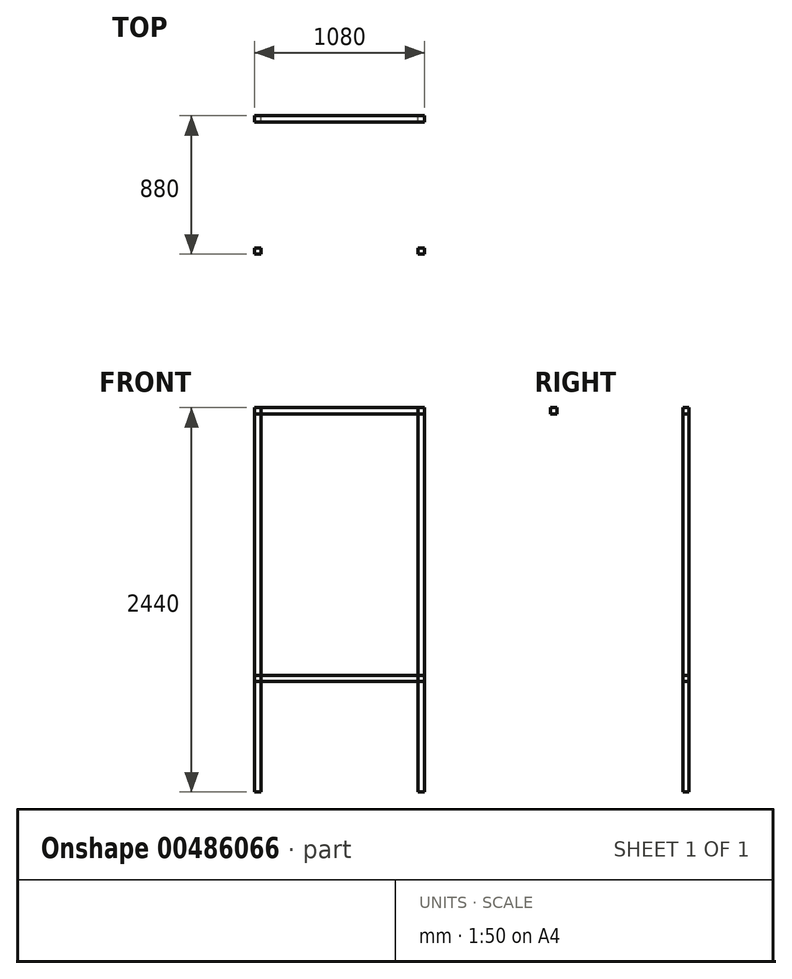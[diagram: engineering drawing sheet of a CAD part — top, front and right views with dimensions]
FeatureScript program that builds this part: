
annotation { "Feature Type Name" : "Feature", "Feature Type Description" : "" }
export const myFeature = defineFeature(function(context is Context, id is Id, definition is map)
    precondition{}
    {
        {
            var Q0;
            Q0=qCreatedBy(makeId("Top.planeOp"),FACE);
            var sketch = newSketch(context, id + "F0", { "sketchPlane" : qUnion([Q0])});
            skLineSegment(sketch, "E0.bottom", {"start": v(119.7, 99.7) * mm, "end": v(1119.7, 99.7) * mm});
            skLineSegment(sketch, "E0.left", {"start": v(119.7, 99.7) * mm, "end": v(119.7, 179.7) * mm});
            skLineSegment(sketch, "E0.right", {"start": v(1119.7, 99.7) * mm, "end": v(1119.7, 179.7) * mm});
            skLineSegment(sketch, "E1.bottom", {"start": v(1119.7, 99.7) * mm, "end": v(119.7, 99.7) * mm});
            skLineSegment(sketch, "E1.top", {"start": v(1119.7, 899.7) * mm, "end": v(119.7, 899.7) * mm});
            skLineSegment(sketch, "E1.left", {"start": v(1119.7, 99.7) * mm, "end": v(1119.7, 899.7) * mm});
            skLineSegment(sketch, "E1.right", {"start": v(119.7, 99.7) * mm, "end": v(119.7, 899.7) * mm});
            skLineSegment(sketch, "E2.0", {"start": v(1159.7, 939.7) * mm, "end": v(79.7, 939.7) * mm});
            skLineSegment(sketch, "E2.1", {"start": v(79.7, 59.7) * mm, "end": v(79.7, 939.7) * mm});
            skLineSegment(sketch, "E3.0", {"start": v(1159.7, 59.7) * mm, "end": v(79.7, 59.7) * mm});
            skLineSegment(sketch, "E4.0", {"start": v(1159.7, 59.7) * mm, "end": v(1159.7, 939.7) * mm});
            skLineSegment(sketch, "E5.bottom", {"start": v(79.7, 59.7) * mm, "end": v(119.7, 59.7) * mm});
            skLineSegment(sketch, "E5.top", {"start": v(79.7, 99.7) * mm, "end": v(119.7, 99.7) * mm});
            skLineSegment(sketch, "E5.left", {"start": v(79.7, 59.7) * mm, "end": v(79.7, 99.7) * mm});
            skLineSegment(sketch, "E5.right", {"start": v(119.7, 59.7) * mm, "end": v(119.7, 99.7) * mm});
            skLineSegment(sketch, "E6.bottom", {"start": v(1159.7, 59.7) * mm, "end": v(1119.7, 59.7) * mm});
            skLineSegment(sketch, "E6.top", {"start": v(1159.7, 99.7) * mm, "end": v(1119.7, 99.7) * mm});
            skLineSegment(sketch, "E6.left", {"start": v(1159.7, 59.7) * mm, "end": v(1159.7, 99.7) * mm});
            skLineSegment(sketch, "E6.right", {"start": v(1119.7, 59.7) * mm, "end": v(1119.7, 99.7) * mm});
            skLineSegment(sketch, "E7.bottom", {"start": v(1119.7, 899.7) * mm, "end": v(1159.7, 899.7) * mm});
            skLineSegment(sketch, "E7.top", {"start": v(1119.7, 939.7) * mm, "end": v(1159.7, 939.7) * mm});
            skLineSegment(sketch, "E7.left", {"start": v(1119.7, 899.7) * mm, "end": v(1119.7, 939.7) * mm});
            skLineSegment(sketch, "E7.right", {"start": v(1159.7, 899.7) * mm, "end": v(1159.7, 939.7) * mm});
            skLineSegment(sketch, "E8.bottom", {"start": v(119.7, 899.7) * mm, "end": v(79.7, 899.7) * mm});
            skLineSegment(sketch, "E8.top", {"start": v(119.7, 939.7) * mm, "end": v(79.7, 939.7) * mm});
            skLineSegment(sketch, "E8.left", {"start": v(119.7, 899.7) * mm, "end": v(119.7, 939.7) * mm});
            skLineSegment(sketch, "E8.right", {"start": v(79.7, 899.7) * mm, "end": v(79.7, 939.7) * mm});
            skSolve(sketch);
        }
        {
            var Q0;
            {var subQ3=sQuery(id+"F0.wireOp",EDGE,"E1.bottom");Q0=makeQuery(id+"F0.imprint","IMPRINT",FACE,{"disambiguationData":[TD([[makeQuery(id+"F0.imprint","IMPRINT",EDGE,{"derivedFrom":subQ3}),1.0]])]});}
            var Q1;
            Q1=makeQuery(id+"F0.imprint","IMPRINT",FACE,{"disambiguationData":[TD([[makeQuery(id+"F0.imprint","IMPRINT",EDGE,{"derivedFrom":sQuery(id+"F0.wireOp",EDGE,"E7.bottom")}),1.0]])]});
            var Q2;
            Q2=makeQuery(id+"F0.imprint","IMPRINT",FACE,{"disambiguationData":[TD([[makeQuery(id+"F0.imprint","IMPRINT",EDGE,{"derivedFrom":sQuery(id+"F0.wireOp",EDGE,"E1.top")}),-1.0]])]});
            var Q3;
            Q3=makeQuery(id+"F0.imprint","IMPRINT",FACE,{"disambiguationData":[TD([[makeQuery(id+"F0.imprint","IMPRINT",EDGE,{"derivedFrom":sQuery(id+"F0.wireOp",EDGE,"E4.0")}),1.0]])]});
            var Q4;
            Q4=makeQuery(id+"F0.imprint","IMPRINT",FACE,{"disambiguationData":[TD([[makeQuery(id+"F0.imprint","IMPRINT",EDGE,{"derivedFrom":sQuery(id+"F0.wireOp",EDGE,"E6.bottom")}),-1.0]])]});
            var Q5;
            Q5=makeQuery(id+"F0.imprint","IMPRINT",FACE,{"disambiguationData":[TD([[makeQuery(id+"F0.imprint","IMPRINT",EDGE,{"derivedFrom":sQuery(id+"F0.wireOp",EDGE,"E8.bottom")}),-1.0]])]});
            var Q6;
            Q6=makeQuery(id+"F0.imprint","IMPRINT",FACE,{"disambiguationData":[TD([[makeQuery(id+"F0.imprint","IMPRINT",EDGE,{"derivedFrom":sQuery(id+"F0.wireOp",EDGE,"E2.1")}),-1.0]])]});
            var Q7;
            Q7=makeQuery(id+"F0.imprint","IMPRINT",FACE,{"disambiguationData":[TD([[makeQuery(id+"F0.imprint","IMPRINT",EDGE,{"derivedFrom":sQuery(id+"F0.wireOp",EDGE,"E5.bottom")}),1.0]])]});
            extrude(context, id + "F1", {"entities" : qUnion([Q0, Q1, Q2, Q3, Q4, Q5, Q6, Q7]), "depth" : 40 * mm, "offsetDistance" : 25 * mm});
        }
        {
            var Q0;
            Q0=makeQuery(id+"F0.imprint","IMPRINT",FACE,{"disambiguationData":[TD([[makeQuery(id+"F0.imprint","IMPRINT",EDGE,{"derivedFrom":sQuery(id+"F0.wireOp",EDGE,"E8.bottom")}),-1.0]])]});
            var Q1;
            Q1=makeQuery(id+"F0.imprint","IMPRINT",FACE,{"disambiguationData":[TD([[makeQuery(id+"F0.imprint","IMPRINT",EDGE,{"derivedFrom":sQuery(id+"F0.wireOp",EDGE,"E7.bottom")}),1.0]])]});
            var Q2;
            Q2=makeQuery(id+"F0.imprint","IMPRINT",FACE,{"disambiguationData":[TD([[makeQuery(id+"F0.imprint","IMPRINT",EDGE,{"derivedFrom":sQuery(id+"F0.wireOp",EDGE,"E6.bottom")}),-1.0]])]});
            var Q3;
            Q3=makeQuery(id+"F0.imprint","IMPRINT",FACE,{"disambiguationData":[TD([[makeQuery(id+"F0.imprint","IMPRINT",EDGE,{"derivedFrom":sQuery(id+"F0.wireOp",EDGE,"E5.bottom")}),1.0]])]});
            extrude(context, id + "F2", {"entities" : qUnion([Q0, Q1, Q2, Q3]), "oppositeDirection" : true, "depth" : 2400 * mm, "offsetDistance" : 25 * mm});
        }
        {
            var Q0;
            Q0=makeQuery(id+"F1.opExtrude","SWEPT_BODY",BODY,{"disambiguationData":[OSD([sQuery(id+"F0.wireOp",EDGE,"E1.bottom"),sQuery(id+"F0.wireOp",EDGE,"E1.top"),sQuery(id+"F0.wireOp",EDGE,"E1.left"),sQuery(id+"F0.wireOp",EDGE,"E1.right"),sQuery(id+"F0.wireOp",EDGE,"E2.0"),sQuery(id+"F0.wireOp",EDGE,"E2.1"),sQuery(id+"F0.wireOp",EDGE,"E3.0"),sQuery(id+"F0.wireOp",EDGE,"E4.0"),sQuery(id+"F0.wireOp",EDGE,"E5.bottom"),sQuery(id+"F0.wireOp",EDGE,"E5.left"),sQuery(id+"F0.wireOp",EDGE,"E6.bottom"),sQuery(id+"F0.wireOp",EDGE,"E6.left"),sQuery(id+"F0.wireOp",EDGE,"E7.top"),sQuery(id+"F0.wireOp",EDGE,"E7.right"),sQuery(id+"F0.wireOp",EDGE,"E8.top"),sQuery(id+"F0.wireOp",EDGE,"E8.right")])]});
            transform(context, id + "F3", {"entities" : qUnion([Q0]), "transformType" : TransformType.TRANSLATION_3D, "dx" : 0 * mm, "dy" : 0 * mm, "dz" : -1700 * mm, "makeCopy" : true});
        }
    });
